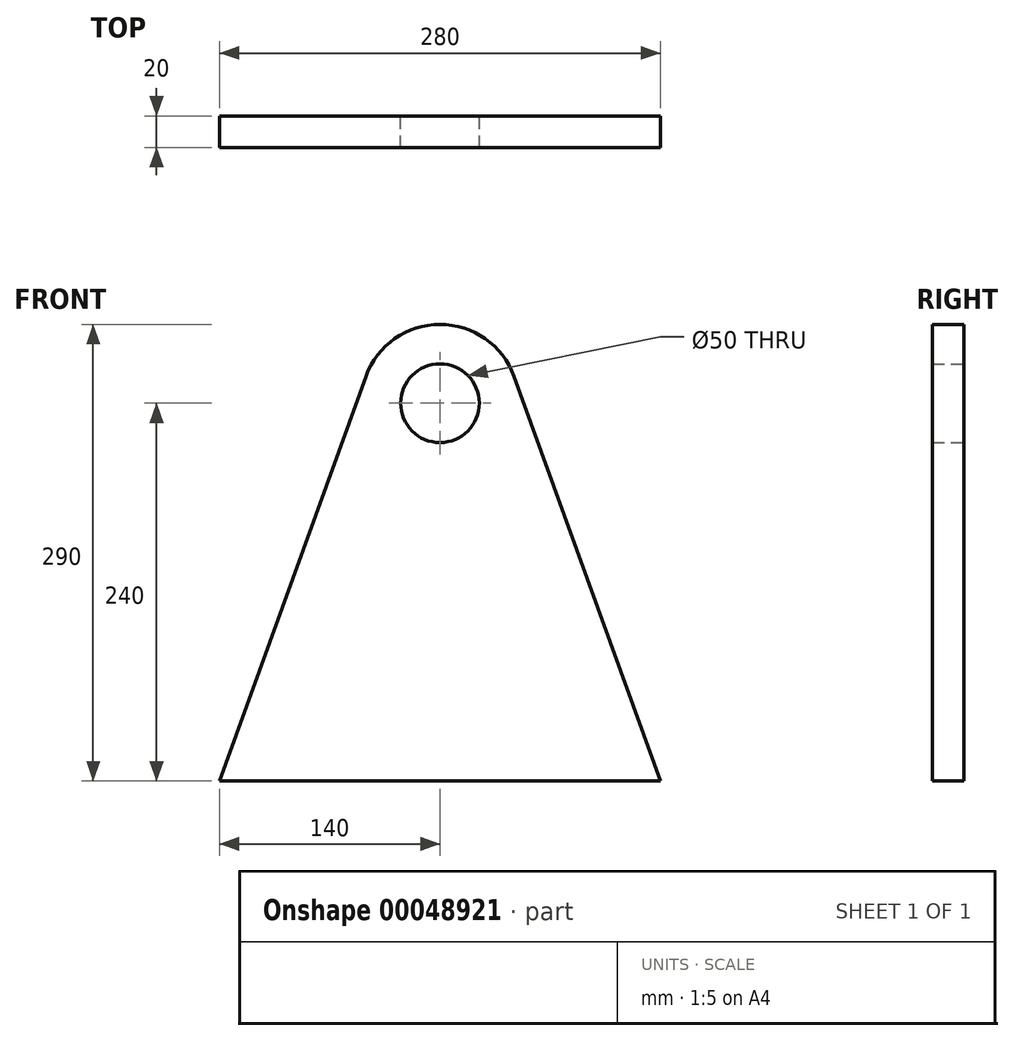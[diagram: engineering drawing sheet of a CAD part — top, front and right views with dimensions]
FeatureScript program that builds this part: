
annotation { "Feature Type Name" : "Feature", "Feature Type Description" : "" }
export const myFeature = defineFeature(function(context is Context, id is Id, definition is map)
    precondition{}
    {
        {
            var Q0;
            Q0=qCreatedBy(makeId("Front.planeOp"),FACE);
            var sketch = newSketch(context, id + "F0", { "sketchPlane" : qUnion([Q0])});
            skLineSegment(sketch, "E0.rect.bottom", {"start": v(140, 120) * mm, "end": v(-140, 120) * mm, "construction": true});
            skLineSegment(sketch, "E0.rect.top", {"start": v(140, -120) * mm, "end": v(-140, -120) * mm});
            skLineSegment(sketch, "E0.rect.left", {"start": v(140, 120) * mm, "end": v(140, -120) * mm, "construction": true});
            skLineSegment(sketch, "E0.rect.right", {"start": v(-140, 120) * mm, "end": v(-140, -120) * mm, "construction": true});
            skPoint(sketch, "E0.rect.middle", {"position": v(0, 0) * mm});
            skLineSegment(sketch, "E1", {"start": v(0, -120) * mm, "end": v(0, 120) * mm, "construction": true});
            skArc(sketch, "E2", {"start": v(47.02, 137.01) * mm, "mid": v(0, 170) * mm, "end": v(-47.02, 137.01) * mm});
            skCircle(sketch, "E3", {"center": v(0, 120) * mm, "radius": 25 * mm});
            skLineSegment(sketch, "E4", {"start": v(-140, -120) * mm, "end": v(-47.02, 137.01) * mm});
            skLineSegment(sketch, "E5.MirrorCS", {"start": v(140, -120) * mm, "end": v(47.02, 137.01) * mm});
            skSolve(sketch);
        }
        {
            var Q0;
            Q0=makeQuery(id+"F0.imprint","IMPRINT",FACE,{"disambiguationData":[TD([[makeQuery(id+"F0.imprint","IMPRINT",EDGE,{"derivedFrom":sQuery(id+"F0.wireOp",EDGE,"E0.rect.top")}),-1.0]])]});
            extrude(context, id + "F1", {"entities" : qUnion([Q0]), "depth" : 20 * mm});
        }
    });
